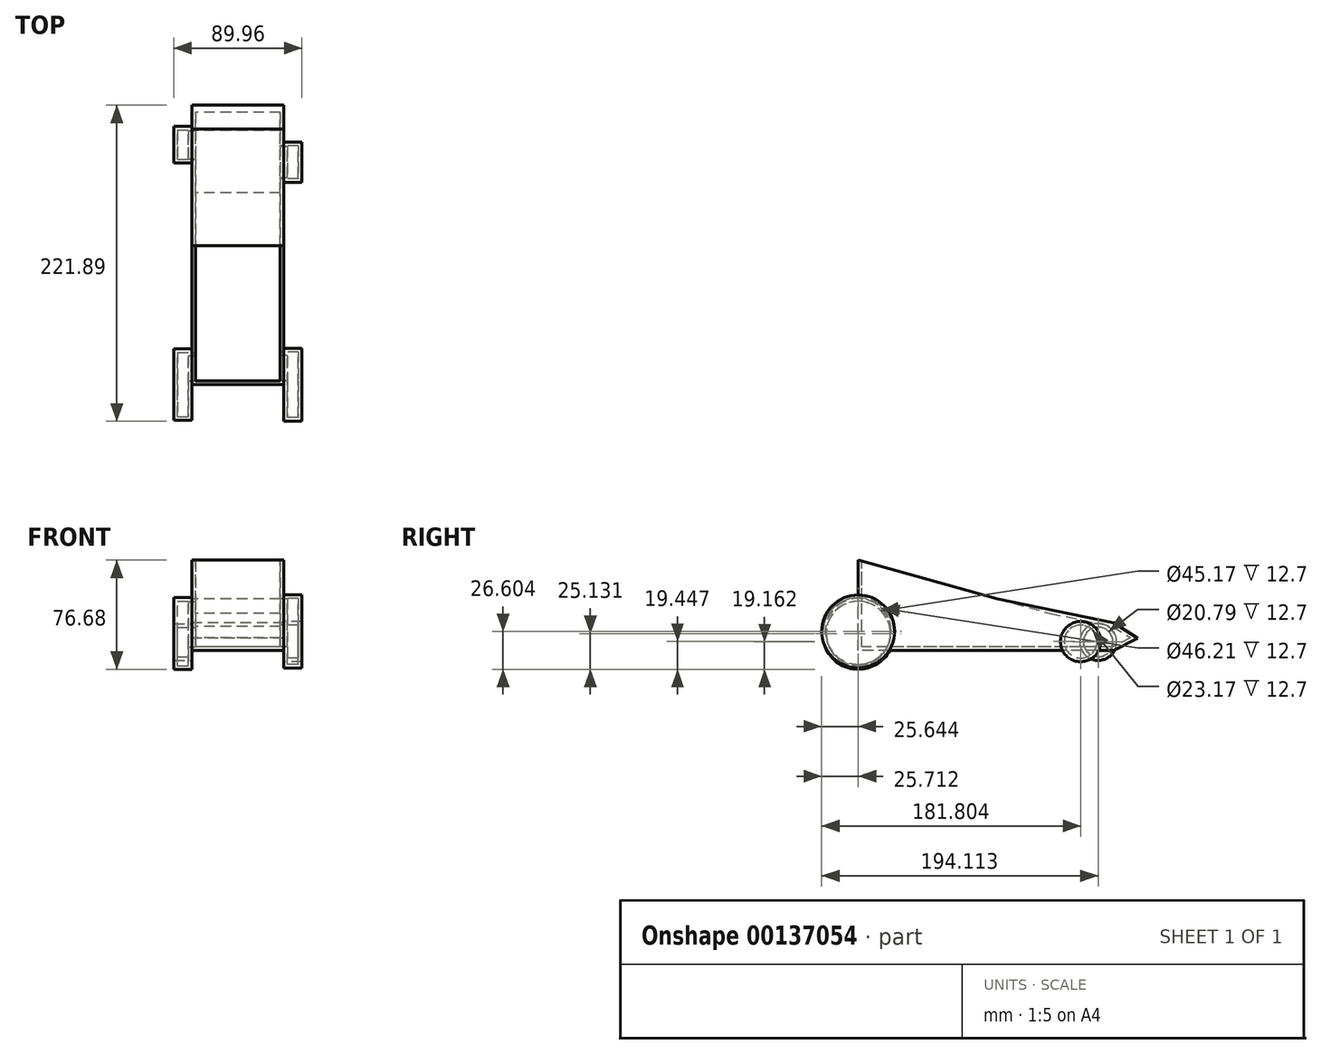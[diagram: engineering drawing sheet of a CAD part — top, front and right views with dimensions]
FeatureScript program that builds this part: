
annotation { "Feature Type Name" : "Feature", "Feature Type Description" : "" }
export const myFeature = defineFeature(function(context is Context, id is Id, definition is map)
    precondition{}
    {
        {
            var Q0;
            Q0=qCreatedBy(makeId("Right.planeOp"),FACE);
            var sketch = newSketch(context, id + "F0", { "sketchPlane" : qUnion([Q0])});
            skLineSegment(sketch, "E0", {"start": v(-97.68, 27.14) * mm, "end": v(0, 0) * mm});
            skLineSegment(sketch, "E1", {"start": v(0, 0) * mm, "end": v(81.77, -16.99) * mm});
            skLineSegment(sketch, "E2", {"start": v(81.77, -16.99) * mm, "end": v(98.57, -27.59) * mm});
            skLineSegment(sketch, "E3", {"start": v(98.57, -27.59) * mm, "end": v(81.77, -36.43) * mm});
            skLineSegment(sketch, "E4", {"start": v(81.77, -36.43) * mm, "end": v(-97.68, -36.43) * mm});
            skLineSegment(sketch, "E5", {"start": v(-97.68, -36.43) * mm, "end": v(-97.68, 0) * mm});
            skLineSegment(sketch, "E6", {"start": v(-97.68, 0) * mm, "end": v(-97.68, 27.14) * mm});
            skSolve(sketch);
        }
        {
            var Q0;
            Q0=makeQuery(id+"F0.imprint","IMPRINT",FACE,{"disambiguationData":[TD([[makeQuery(id+"F0.imprint","IMPRINT",EDGE,{"derivedFrom":sQuery(id+"F0.wireOp",EDGE,"E0")}),-1.0]])]});
            extrude(context, id + "F1", {"entities" : qUnion([Q0]), "depth" : 64.56 * mm});
        }
        {
            var Q0;
            Q0=qCreatedBy(makeId("Right.planeOp"),FACE);
            var sketch = newSketch(context, id + "F2", { "sketchPlane" : qUnion([Q0])});
            skCircle(sketch, "E7", {"center": v(-97.6, -24.4) * mm, "radius": 25.13 * mm});
            skCircle(sketch, "E8", {"center": v(70.8, -30.38) * mm, "radius": 12.93 * mm});
            skSolve(sketch);
        }
        {
            var Q0;
            Q0=makeQuery(id+"F2.imprint","IMPRINT",FACE,{"disambiguationData":[TD([[makeQuery(id+"F2.imprint","IMPRINT",EDGE,{"derivedFrom":sQuery(id+"F2.wireOp",EDGE,"E7")}),1.0]])]});
            var Q1;
            Q1=makeQuery(id+"F2.imprint","IMPRINT",FACE,{"disambiguationData":[TD([[makeQuery(id+"F2.imprint","IMPRINT",EDGE,{"derivedFrom":sQuery(id+"F2.wireOp",EDGE,"E8")}),1.0]])]});
            extrude(context, id + "F3", {"entities" : qUnion([Q0, Q1]), "operationType" : NewBodyOperationType.ADD, "oppositeDirection" : true, "depth" : 12.7 * mm});
        }
        {
            var Q0;
            Q0=makeQuery(id+"F1.opExtrude","CAP_FACE",FACE,{"disambiguationData":[OSD([sQuery(id+"F0.wireOp",EDGE,"E0"),sQuery(id+"F0.wireOp",EDGE,"E1"),sQuery(id+"F0.wireOp",EDGE,"E2"),sQuery(id+"F0.wireOp",EDGE,"E3"),sQuery(id+"F0.wireOp",EDGE,"E4"),sQuery(id+"F0.wireOp",EDGE,"E5"),sQuery(id+"F0.wireOp",EDGE,"E6")])],"isStart":false});
            var sketch = newSketch(context, id + "F4", { "sketchPlane" : qUnion([Q0])});
            skCircle(sketch, "E9", {"center": v(-97.68, -22.94) * mm, "radius": 25.64 * mm});
            skCircle(sketch, "E10", {"center": v(58.48, -30.1) * mm, "radius": 14.12 * mm});
            skSolve(sketch);
        }
        {
            var Q0;
            Q0 = qSketchRegion(id + "F4", true);
            extrude(context, id + "F5", {"entities" : qUnion([Q0]), "operationType" : NewBodyOperationType.ADD, "depth" : 12.7 * mm});
        }
        {
            var Q0;
            Q0=makeQuery(id+"F1.opExtrude","SWEPT_FACE",FACE,{"disambiguationData":[OSD([sQuery(id+"F0.wireOp",EDGE,"E0")])]});
            shell(context, id + "F6", {"entities" : qUnion([Q0]), "thickness" : 2.54 * mm});
        }
    });
